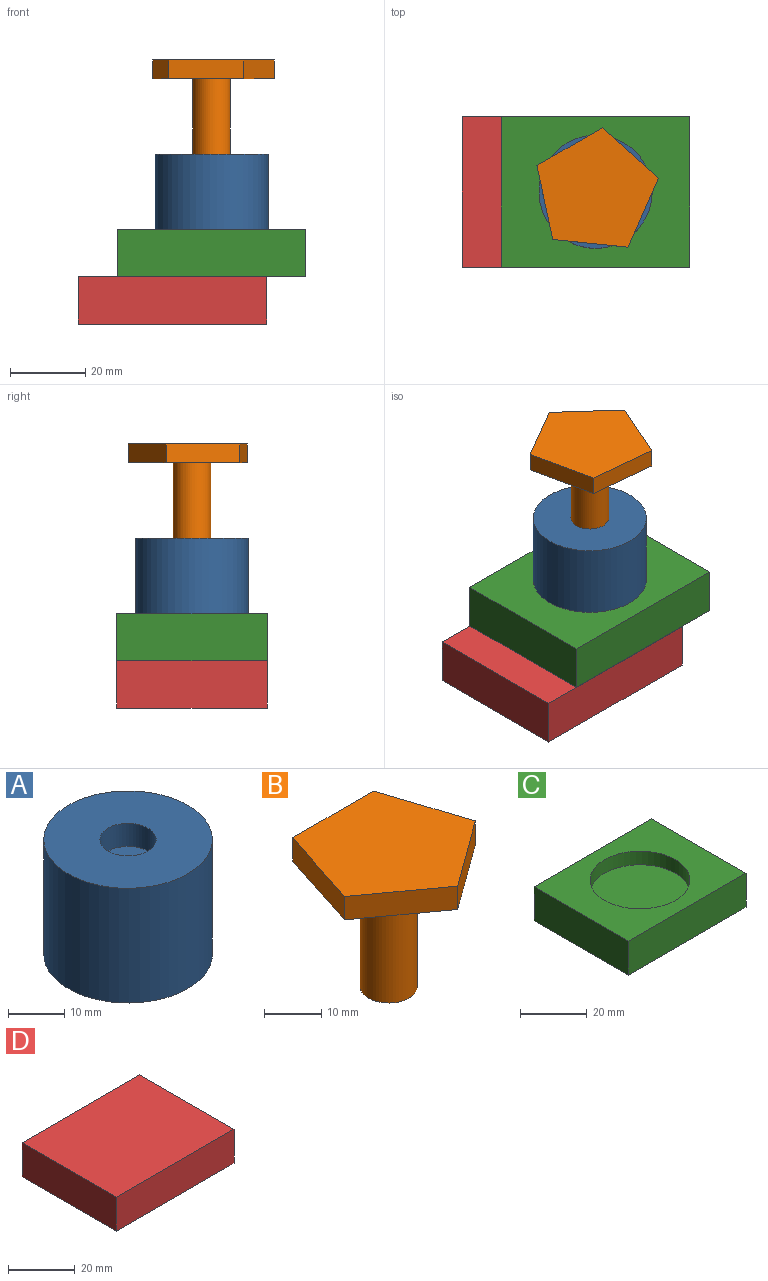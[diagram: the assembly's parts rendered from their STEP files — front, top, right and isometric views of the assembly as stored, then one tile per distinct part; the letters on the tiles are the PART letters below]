
ASSEMBLY  parts=4 mates=3
PART A: 5 faces, bbox 30x30x25 mm
  f0: cylinder r=15mm len=30mm, axis (0,0,-1), area 2356.2mm2, adj f1,f2
  f1: plane 30x30mm, normal (0,0,1), area 628.3mm2, adj f0,f3
  f2: plane 30x30mm, normal (0,0,-1), area 706.9mm2, adj f0
  f3: cylinder r=5mm len=10mm, axis (0,0,1), area 157.1mm2, adj f1,f4
  f4: plane 10x10mm, normal (0,0,1), area 78.5mm2, adj f3
PART B: 9 faces, bbox 32.4x30.8x30 mm
  f0: cylinder r=5mm len=25mm, axis (0,0,-1), area 785.4mm2, adj f1,f8
  f1: plane 10x10mm, normal (0,0,-1), area 78.5mm2, adj f0
  f2: plane 19.02x6.18mm, normal (0.95,0.31,0), area 100mm2, adj f3,f6,f7,f8
  f3: plane 20x5mm, normal (0,1,0), area 100mm2, adj f2,f4,f7,f8
  f4: plane 19.02x6.18mm, normal (-0.95,0.31,0), area 100mm2, adj f3,f5,f7,f8
  f5: plane 16.18x11.76mm, normal (-0.59,-0.81,0), area 100mm2, adj f4,f6,f7,f8
  f6: plane 16.18x11.76mm, normal (0.59,-0.81,0), area 100mm2, adj f2,f5,f7,f8
  f7: plane 32.36x30.78mm, normal (0,0,1), area 688.2mm2, adj f2,f3,f4,f5,f6
  f8: plane 32.36x30.78mm, normal (0,0,-1), area 609.7mm2, adj f0,f2,f3,f4,f5,f6
PART C: 8 faces, bbox 50x40x12.5 mm
  f0: plane 50x12.5mm, normal (0,-1,0), area 625mm2, adj f1,f3,f4,f5
  f1: plane 40x12.5mm, normal (1,0,0), area 500mm2, adj f0,f2,f4,f5
  f2: plane 50x12.5mm, normal (0,1,0), area 625mm2, adj f1,f3,f4,f5
  f3: plane 40x12.5mm, normal (-1,0,0), area 500mm2, adj f0,f2,f4,f5
  f4: plane 50x40mm, normal (0,0,1), area 1293.1mm2, adj f0,f1,f2,f3,f6
  f5: plane 50x40mm, normal (0,0,-1), area 2000mm2, adj f0,f1,f2,f3
  f6: cylinder r=15mm len=30mm, axis (0,0,1), area 471.2mm2, adj f4,f7
  f7: plane 30x30mm, normal (0,0,1), area 706.9mm2, adj f6
PART D: 6 faces, bbox 50x40x12.5 mm
  f0: plane 50x40mm, normal (0,0,1), area 2000mm2, adj f2,f3,f4,f5
  f1: plane 50x40mm, normal (0,0,-1), area 2000mm2, adj f2,f3,f4,f5
  f2: plane 40x12.5mm, normal (-1,0,0), area 500mm2, adj f0,f1,f3,f5
  f3: plane 50x12.5mm, normal (0,1,0), area 625mm2, adj f0,f1,f2,f4
  f4: plane 40x12.5mm, normal (1,0,0), area 500mm2, adj f0,f1,f3,f5
  f5: plane 50x12.5mm, normal (0,-1,0), area 625mm2, adj f0,f1,f2,f4
PLACE A at identity
PLACE B rot(axis=(0,0,1),174.2deg) t=(0,0,0)mm
PLACE C at identity fixed
PLACE D t=(-10.39,0,0)mm
MATE fastened C.f6 <-> A.f0  axis (0,0,1) through (0,0,20)mm
MATE slider D.f4 <-> C.f1  axis (1,0,0) through (14.61,0,12.5)mm
MATE revolute B.f0 <-> A.f3  axis (0,0,-1) through (0,0,40)mm
